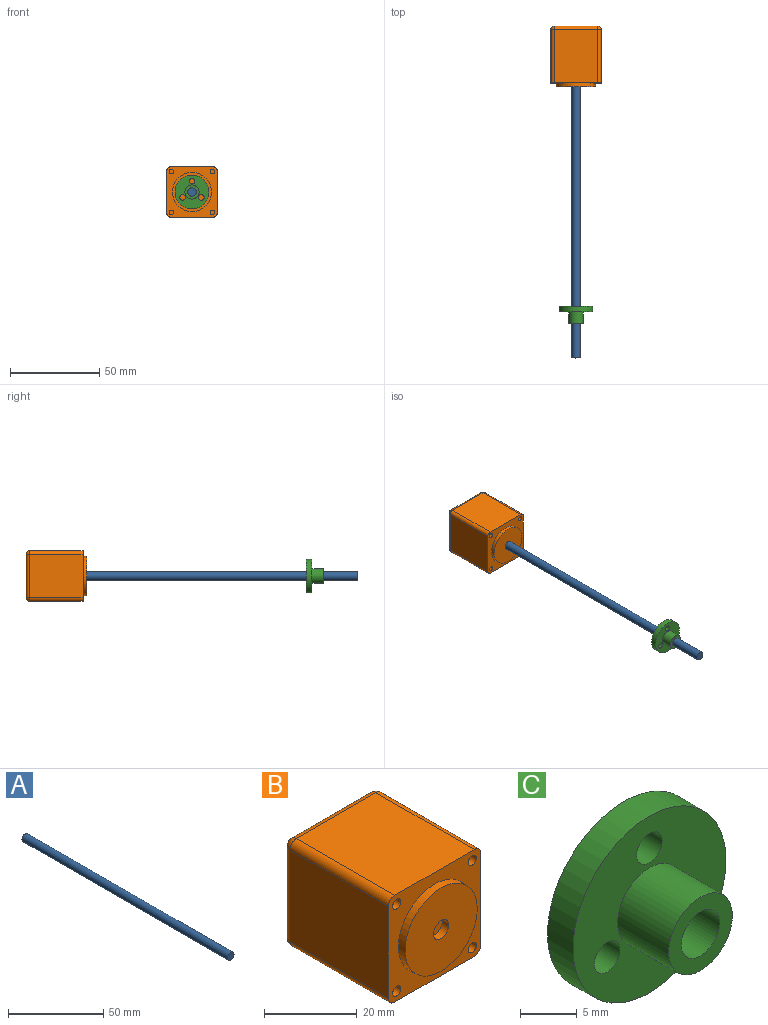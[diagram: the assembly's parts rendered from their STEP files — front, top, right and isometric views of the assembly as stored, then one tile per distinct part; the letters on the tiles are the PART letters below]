
ASSEMBLY  parts=3 mates=2
PART A: 3 faces, bbox 4.8x152.4x4.8 mm
  f0: cylinder r=2.38mm len=152.4mm, axis (0,1,0), area 2279mm2, adj f1,f2
  f1: plane 4.76x4.76mm, normal (0,-1,0), area 17.8mm2, adj f0
  f2: plane 4.76x4.76mm, normal (0,1,0), area 17.8mm2, adj f0
PART B: 30 faces, bbox 28.2x34x28.2 mm
  f0: plane 30x24.2mm, normal (0,0,-1), area 726mm2, adj f5,f23,f27,f29
  f1: plane 30x24.2mm, normal (1,0,0), area 726mm2, adj f5,f20,f26,f29
  f2: plane 30x24.2mm, normal (0,0,1), area 726mm2, adj f5,f18,f20,f21
  f3: plane 30x24.2mm, normal (-1,0,0), area 726mm2, adj f5,f18,f22,f23
  f4: plane 24.2x24.2mm, normal (0,1,0), area 585.6mm2, adj f21,f22,f26,f27
  f5: plane 28.2x28.2mm, normal (0,-1,0), area 392mm2, adj f0,f1,f2,f3,f7,f10,f12,f14
  f6: cylinder r=2.38mm len=4.76mm, axis (0,1,0), area 29.9mm2, adj f8,f9
  f7: cylinder r=11mm len=22mm, axis (0,1,0), area 138.2mm2, adj f5,f8
  f8: plane 22x22mm, normal (0,-1,0), area 362.3mm2, adj f6,f7
  f9: plane 4.76x4.76mm, normal (0,-1,0), area 17.8mm2, adj f6
  f10: cylinder r=1.25mm len=3mm, axis (0,-1,0), area 23.6mm2, adj f5,f11
  f11: plane 2.5x2.5mm, normal (0,-1,0), area 4.9mm2, adj f10
  f12: cylinder r=1.25mm len=3mm, axis (0,-1,0), area 23.6mm2, adj f5,f13
  f13: plane 2.5x2.5mm, normal (0,-1,0), area 4.9mm2, adj f12
  f14: cylinder r=1.25mm len=3mm, axis (0,-1,0), area 23.6mm2, adj f5,f15
  f15: plane 2.5x2.5mm, normal (0,-1,0), area 4.9mm2, adj f14
  f16: cylinder r=1.25mm len=3mm, axis (0,-1,0), area 23.6mm2, adj f5,f17
  f17: plane 2.5x2.5mm, normal (0,-1,0), area 4.9mm2, adj f16
  f18: cylinder r=2mm len=30mm, axis (0,-1,0), area 94.2mm2, adj f2,f3,f5,f19
  f19: sphere r=2mm, area 6.3mm2, adj f18,f21,f22
  f20: cylinder r=2mm len=30mm, axis (0,1,0), area 94.2mm2, adj f1,f2,f5,f24
  f21: cylinder r=2mm len=24.2mm, axis (1,0,0), area 76mm2, adj f2,f4,f19,f24
  f22: cylinder r=2mm len=24.2mm, axis (0,0,1), area 76mm2, adj f3,f4,f19,f25
  f23: cylinder r=2mm len=30mm, axis (0,1,0), area 94.2mm2, adj f0,f3,f5,f25
  f24: sphere r=2mm, area 6.3mm2, adj f20,f21,f26
  f25: sphere r=2mm, area 6.3mm2, adj f22,f23,f27
  f26: cylinder r=2mm len=24.2mm, axis (0,0,-1), area 76mm2, adj f1,f4,f24,f28
  f27: cylinder r=2mm len=24.2mm, axis (-1,0,0), area 76mm2, adj f0,f4,f25,f28
  f28: sphere r=2mm, area 6.3mm2, adj f26,f27,f29
  f29: cylinder r=2mm len=30mm, axis (0,-1,0), area 94.2mm2, adj f0,f1,f5,f28
PART C: 9 faces, bbox 19.1x9.5x19.1 mm
  f0: cylinder r=2.38mm len=9.53mm, axis (0,1,0), area 142.5mm2, adj f2,f3
  f1: cylinder r=3.97mm len=7.94mm, axis (0,1,0), area 158.4mm2, adj f2,f8
  f2: plane 7.94x7.94mm, normal (0,-1,0), area 31.7mm2, adj f0,f1
  f3: plane 19.05x19.05mm, normal (0,1,0), area 243.4mm2, adj f0,f4,f5,f6,f7
  f4: cylinder r=1.59mm len=3.18mm, axis (0,1,0), area 31.8mm2, adj f3,f8
  f5: cylinder r=1.59mm len=3.18mm, axis (0,1,0), area 31.8mm2, adj f3,f8
  f6: cylinder r=1.59mm len=3.18mm, axis (0,1,0), area 31.8mm2, adj f3,f8
  f7: cylinder r=9.53mm len=19.05mm, axis (0,1,0), area 190.3mm2, adj f3,f8
  f8: plane 19.05x19.05mm, normal (0,-1,0), area 211.7mm2, adj f1,f4,f5,f6,f7
PLACE A t=(-0.02,-0.01,0.17)mm
PLACE B t=(-0.02,1.99,0.17)mm fixed
PLACE C t=(-0.02,-121.39,0.17)mm
MATE cylindrical C.f0 <-> A.f0  axis (0,1,0) through (-0.02,-132.92,0.17)mm
MATE revolute A.f0 <-> B.f6  axis (0,1,0) through (-0.02,-0.01,0.17)mm
